# Revit family: sicompact_r__31_micro___pl32_5xa7561a2k23_d3a6
name_source: partatom
category: Lighting Fixtures
units: mm (PartAtom-declared; Revit-internal decimal feet)

## family parameters
Cut with Voids When Loaded = No
Host = Face
Light Source = No
Part Type = Normal
Room Calculation Point = No
Round Connector Dimension = Use Diameter
Shared = No

## types (1)
- SiCompact® 31 micro  PL32 (1 x LED, 4400 lm, 29 W, 4000K)
    Apparent Load = 29 VA
    CIE Flux Codes = 32 69 98 100 100
    Color Rendering = 70
    Color Temperature = 4000K
    Default Elevation = 1800 mm
    Description = SiCompact® 31 micro, floodlight, primary light control with lens, of plastic, of toughened safety glass, transparent, light distribution: PL32, light emission: direct distribution, primary light characteristic: asymmetric, installation type: surface-mounted, LED, High Power LED, rated luminous flux: 4.400lm, luminous efficacy: 152lm/W, light colour: 740, colour temperature: 4000K, control gear: ECG, with cable, 3x 1.5mm², mains connection: 220..240V, AC, 50/60Hz, connection cable pre-assembled, cable length: 2m, rated input power: 29W, of diecast aluminium, specular, metallic grey (RAL 9006), length: 330mm, width: 159mm, height: 47mm, bracket, of sheet steel, coated, metallic grey (RAL 9006), ON/OFF, protection rating (complete): IP66, insulation class (complete): insulation class I (protective earthing), certification: CE, impact resistance: IK08, permissible operating ambient temperature: -40..+45°C, packaging unit: 1 piece

Light Distribution: PL32
    Height = 46 mm
    Lamp = 1 x LED
    Lamp Light Flux = 4400 lm
    Lamp Power = 29 W
    Lamp count = 1
    Length = 310 mm
    Luminous efficacy = 152 lm/W
    Manufacturer = Siteco
    ModVariant = No
    Model = 5XA7561A2K23
    Number of Poles = 1
    OnlyDefault = Yes
    Power Factor = 1
    Product Name = SiCompact® 31 micro | PL32
    Product group = floodlight | pylon top
    ProductGroupID = 6101
    Protection Class = Protection class I
    Protection Degree = IP 66
    RLX_Detail_Level = 1
    RlxData = <blob elided: 115961 chars, md5=c54bc2b1>
    Socket = socket
    Standby Power = 0 W
    System Light Flux = 4400 lm
    System Power = 29 W
    Type Comments = Product without accessories
    Type Image = l_1004830.jpg
    URL = http://relux.com
    VarID = ---
    Voltage = 0 V
    Weight = 0.00 kg
    Width = 160 mm

## geometry (parser evidence)
native form markers: Sweep x14
no freeform markers — native parametric forms only
